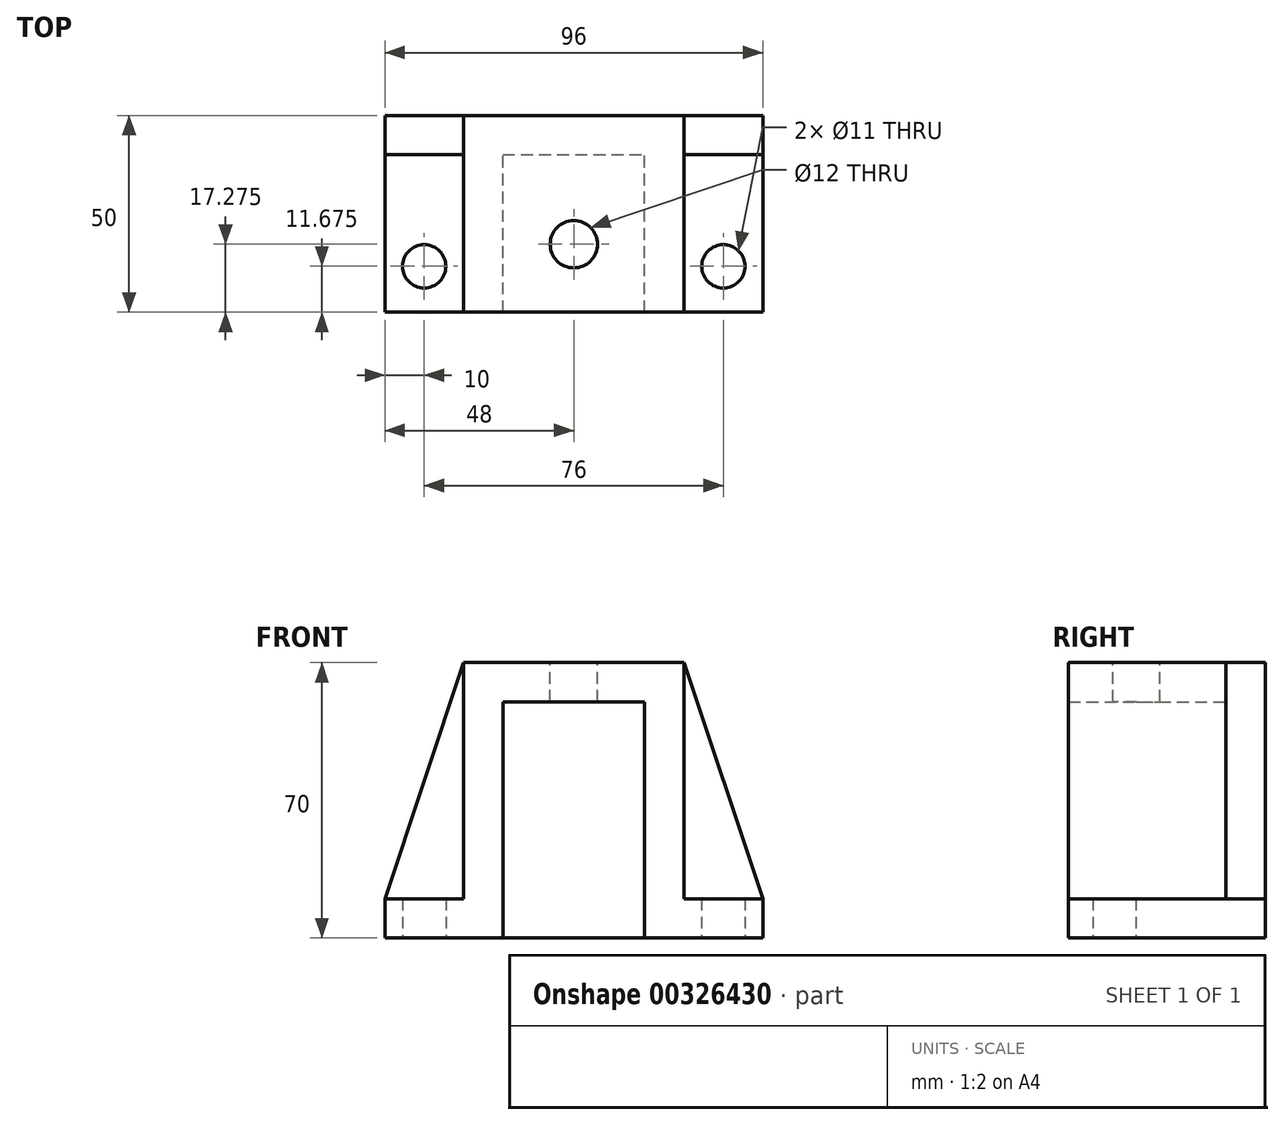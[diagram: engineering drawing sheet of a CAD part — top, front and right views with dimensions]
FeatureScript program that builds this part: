
annotation { "Feature Type Name" : "Feature", "Feature Type Description" : "" }
export const myFeature = defineFeature(function(context is Context, id is Id, definition is map)
    precondition{}
    {
        {
            var Q0;
            Q0=qCreatedBy(makeId("Front.planeOp"),FACE);
            var sketch = newSketch(context, id + "F0", { "sketchPlane" : qUnion([Q0])});
            skLineSegment(sketch, "E0", {"start": v(0, 62.5) * mm, "end": v(0, -47.68) * mm, "construction": true});
            skLineSegment(sketch, "E1", {"start": v(-48, 0) * mm, "end": v(-48, 10) * mm});
            skLineSegment(sketch, "E2", {"start": v(-48, 10) * mm, "end": v(-28, 70) * mm});
            skLineSegment(sketch, "E3", {"start": v(-28, 70) * mm, "end": v(0, 70) * mm});
            skLineSegment(sketch, "E4", {"start": v(-28, 70) * mm, "end": v(-28, 10) * mm});
            skLineSegment(sketch, "E5", {"start": v(-28, 10) * mm, "end": v(-48, 10) * mm});
            skLineSegment(sketch, "E6", {"start": v(-48, 0) * mm, "end": v(0, 0) * mm});
            skLineSegment(sketch, "E7", {"start": v(0, 60) * mm, "end": v(-18, 60) * mm});
            skLineSegment(sketch, "E8", {"start": v(-18, 60) * mm, "end": v(-18, 0) * mm});
            skLineSegment(sketch, "E9.MirrorCS", {"start": v(0, 60) * mm, "end": v(18, 60) * mm});
            skLineSegment(sketch, "E10.MirrorCS", {"start": v(28, 70) * mm, "end": v(0, 70) * mm});
            skLineSegment(sketch, "E11.MirrorCS", {"start": v(28, 70) * mm, "end": v(28, 10) * mm});
            skLineSegment(sketch, "E12.MirrorCS", {"start": v(48, 10) * mm, "end": v(28, 70) * mm});
            skLineSegment(sketch, "E13.MirrorCS", {"start": v(28, 10) * mm, "end": v(48, 10) * mm});
            skLineSegment(sketch, "E14.MirrorCS", {"start": v(48, 0) * mm, "end": v(48, 10) * mm});
            skLineSegment(sketch, "E15.MirrorCS", {"start": v(48, 0) * mm, "end": v(0, 0) * mm});
            skLineSegment(sketch, "E16.MirrorCS", {"start": v(18, 60) * mm, "end": v(18, 0) * mm});
            skSolve(sketch);
        }
        {
            var Q0;
            {var subQ2=sQuery(id+"F0.wireOp",EDGE,"E1");Q0=makeQuery(id+"F0.imprint","IMPRINT",FACE,{"disambiguationData":[TD([[makeQuery(id+"F0.imprint","IMPRINT",EDGE,{"derivedFrom":subQ2}),-1.0]])]});}
            extrude(context, id + "F1", {"entities" : qUnion([Q0]), "depth" : 50 * mm});
        }
        {
            var Q0;
            Q0=makeQuery(id+"F0.imprint","IMPRINT",FACE,{"disambiguationData":[TD([[makeQuery(id+"F0.imprint","IMPRINT",EDGE,{"derivedFrom":sQuery(id+"F0.wireOp",EDGE,"E2")}),-1.0]])]});
            var Q1;
            Q1=makeQuery(id+"F0.imprint","IMPRINT",FACE,{"disambiguationData":[TD([[makeQuery(id+"F0.imprint","IMPRINT",EDGE,{"derivedFrom":sQuery(id+"F0.wireOp",EDGE,"E11.MirrorCS")}),1.0]])]});
            var Q2;
            Q2=makeQuery(id+"F0.imprint","IMPRINT",FACE,{"disambiguationData":[TD([[makeQuery(id+"F0.imprint","IMPRINT",EDGE,{"derivedFrom":sQuery(id+"F0.wireOp",EDGE,"E7")}),1.0]])]});
            extrude(context, id + "F2", {"entities" : qUnion([Q0, Q1, Q2]), "operationType" : NewBodyOperationType.ADD, "depth" : 10 * mm});
        }
        {
            var Q0;
            Q0=qCreatedBy(makeId("Top.planeOp"),FACE);
            var sketch = newSketch(context, id + "F3", { "sketchPlane" : qUnion([Q0])});
            skCircle(sketch, "E17", {"center": v(-38, -38.33) * mm, "radius": 5.5 * mm});
            skCircle(sketch, "E18", {"center": v(38, -38.32) * mm, "radius": 5.5 * mm});
            skSolve(sketch);
        }
        {
            var Q0;
            Q0 = qSketchRegion(id + "F3", true);
            extrude(context, id + "F4", {"entities" : qUnion([Q0]), "operationType" : NewBodyOperationType.REMOVE, "depth" : 10 * mm});
        }
        {
            var Q0;
            Q0=makeQuery(id+"F1.opExtrude","SWEPT_FACE",FACE,{"disambiguationData":[OSD([sQuery(id+"F0.wireOp",EDGE,"E3"),sQuery(id+"F0.wireOp",EDGE,"E10.MirrorCS")])]});
            var sketch = newSketch(context, id + "F5", { "sketchPlane" : qUnion([Q0])});
            skCircle(sketch, "E19", {"center": v(0, -32.73) * mm, "radius": 6 * mm});
            skSolve(sketch);
        }
        {
            var Q0;
            Q0 = qSketchRegion(id + "F5", true);
            extrude(context, id + "F6", {"entities" : qUnion([Q0]), "operationType" : NewBodyOperationType.REMOVE, "oppositeDirection" : true, "depth" : 12 * mm});
        }
    });
